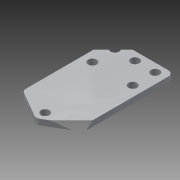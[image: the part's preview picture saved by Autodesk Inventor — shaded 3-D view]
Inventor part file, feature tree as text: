
AUTODESK INVENTOR PART (.ipt)
format: ipt  version: 2014 (Build 180170000, 170)  size: 137,216 bytes
history: native  units: in
note: dims shown in document units (in); Inventor stores cm internally (conversion verified against a paired STEP export)
features: extrude x1, fillet x1, sketch x1
ambient origin geometry x8: Origin, YZ Plane, XZ Plane, XY Plane, X Axis, Y Axis, Z Axis, Center Point
bodies: Solid1 (feature_tree)
feature tree (3):
  extrude  "Extrusion1"  Depth=2.0in
  fillet  "Fillet1"  Radius=0.19in
  sketch  "Sketch1"  dims[d1=0.19in d2=2.0in d3=0.19in d4=0.19in d5=0.5in d6=0.4485in d7=0.4485in d8=0.0in d9=0.19in d10=0.19in d11=0.4485in d12=0.5in d14=0.125in d15=0.125in d16=0.0in d17=1.5in d18=1.35in d19=0.1875in d20=0.25in d21=1.9375in d22=0.3175in d23=0.125in]
